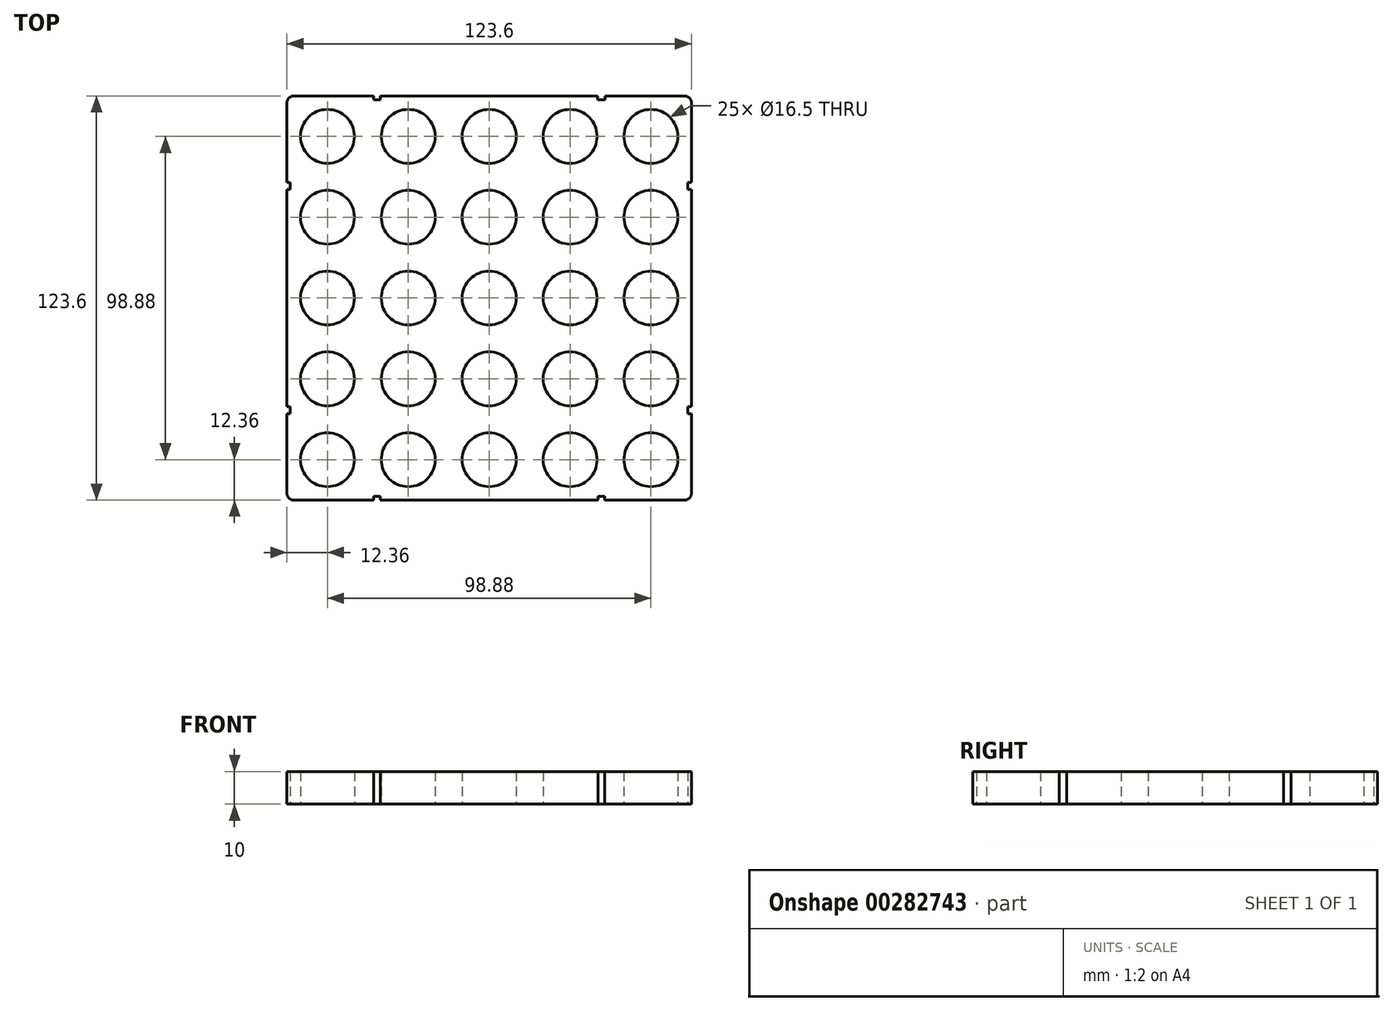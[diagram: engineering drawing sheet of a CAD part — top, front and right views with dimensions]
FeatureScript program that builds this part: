
annotation { "Feature Type Name" : "Feature", "Feature Type Description" : "" }
export const myFeature = defineFeature(function(context is Context, id is Id, definition is map)
    precondition{}
    {
        {
            var Q0;
            Q0=qCreatedBy(makeId("Top.planeOp"),FACE);
            var sketch = newSketch(context, id + "F0", { "sketchPlane" : qUnion([Q0])});
            skLineSegment(sketch, "E0.bottom", {"start": v(59.8, 61.8) * mm, "end": v(-59.8, 61.8) * mm});
            skLineSegment(sketch, "E0.top", {"start": v(59.8, -61.8) * mm, "end": v(-59.8, -61.8) * mm});
            skLineSegment(sketch, "E0.left", {"start": v(61.8, 59.8) * mm, "end": v(61.8, -59.8) * mm});
            skLineSegment(sketch, "E0.right", {"start": v(-61.8, 59.8) * mm, "end": v(-61.8, -59.8) * mm});
            skPoint(sketch, "E0.middle", {"position": v(0, 0) * mm});
            skPoint(sketch, "E1.visualSharp", {"position": v(-61.8, 61.8) * mm});
            skArc(sketch, "E1.filletArc", {"start": v(-59.8, 61.8) * mm, "mid": v(-61.21, 61.21) * mm, "end": v(-61.8, 59.8) * mm});
            skPoint(sketch, "E2.visualSharp", {"position": v(61.8, 61.8) * mm});
            skArc(sketch, "E2.filletArc", {"start": v(61.8, 59.8) * mm, "mid": v(61.21, 61.21) * mm, "end": v(59.8, 61.8) * mm});
            skPoint(sketch, "E3.visualSharp", {"position": v(61.8, -61.8) * mm});
            skArc(sketch, "E3.filletArc", {"start": v(59.8, -61.8) * mm, "mid": v(61.21, -61.21) * mm, "end": v(61.8, -59.8) * mm});
            skPoint(sketch, "E4.visualSharp", {"position": v(-61.8, -61.8) * mm});
            skArc(sketch, "E4.filletArc", {"start": v(-61.8, -59.8) * mm, "mid": v(-61.21, -61.21) * mm, "end": v(-59.8, -61.8) * mm});
            skLineSegment(sketch, "E5", {"start": v(-78.6, 0) * mm, "end": v(67.95, 0) * mm, "construction": true});
            skLineSegment(sketch, "E6", {"start": v(0, 68.22) * mm, "end": v(0, -54.86) * mm, "construction": true});
            skLineSegment(sketch, "E7", {"start": v(-24.72, 68.22) * mm, "end": v(-24.72, -54.86) * mm, "construction": true});
            skLineSegment(sketch, "E8", {"start": v(-49.44, 68.22) * mm, "end": v(-49.44, -54.86) * mm, "construction": true});
            skLineSegment(sketch, "E9", {"start": v(24.72, 68.22) * mm, "end": v(24.72, -54.86) * mm, "construction": true});
            skLineSegment(sketch, "E10", {"start": v(49.44, 68.22) * mm, "end": v(49.44, -54.86) * mm, "construction": true});
            skLineSegment(sketch, "E11", {"start": v(-78.6, 24.72) * mm, "end": v(67.95, 24.72) * mm, "construction": true});
            skLineSegment(sketch, "E12", {"start": v(-78.6, 49.44) * mm, "end": v(67.95, 49.44) * mm, "construction": true});
            skLineSegment(sketch, "E13", {"start": v(-78.6, -24.72) * mm, "end": v(67.95, -24.72) * mm, "construction": true});
            skLineSegment(sketch, "E14", {"start": v(-78.6, -49.44) * mm, "end": v(67.95, -49.44) * mm, "construction": true});
            skCircle(sketch, "E15", {"center": v(-49.44, 49.44) * mm, "radius": 8.25 * mm});
            skCircle(sketch, "E16", {"center": v(-24.72, 49.44) * mm, "radius": 8.25 * mm});
            skCircle(sketch, "E17", {"center": v(0, 49.44) * mm, "radius": 8.25 * mm});
            skCircle(sketch, "E18", {"center": v(24.72, 49.44) * mm, "radius": 8.25 * mm});
            skCircle(sketch, "E19", {"center": v(49.44, 49.44) * mm, "radius": 8.25 * mm});
            skCircle(sketch, "E20", {"center": v(-49.44, 24.72) * mm, "radius": 8.25 * mm});
            skCircle(sketch, "E21", {"center": v(-24.72, 24.72) * mm, "radius": 8.25 * mm});
            skCircle(sketch, "E22", {"center": v(0, 24.72) * mm, "radius": 8.25 * mm});
            skCircle(sketch, "E23", {"center": v(24.72, 24.72) * mm, "radius": 8.25 * mm});
            skCircle(sketch, "E24", {"center": v(49.44, 24.72) * mm, "radius": 8.25 * mm});
            skCircle(sketch, "E25", {"center": v(49.44, 0) * mm, "radius": 8.25 * mm});
            skCircle(sketch, "E26", {"center": v(24.72, 0) * mm, "radius": 8.25 * mm});
            skCircle(sketch, "E27", {"center": v(-49.44, 0) * mm, "radius": 8.25 * mm});
            skCircle(sketch, "E28", {"center": v(-24.72, 0) * mm, "radius": 8.25 * mm});
            skCircle(sketch, "E29", {"center": v(0, 0) * mm, "radius": 8.25 * mm});
            skCircle(sketch, "E30", {"center": v(-49.44, -24.72) * mm, "radius": 8.25 * mm});
            skCircle(sketch, "E31", {"center": v(-49.44, -49.44) * mm, "radius": 8.25 * mm});
            skCircle(sketch, "E32", {"center": v(-24.72, -24.72) * mm, "radius": 8.25 * mm});
            skCircle(sketch, "E33", {"center": v(-24.72, -49.44) * mm, "radius": 8.25 * mm});
            skCircle(sketch, "E34", {"center": v(0, -24.72) * mm, "radius": 8.25 * mm});
            skCircle(sketch, "E35", {"center": v(0, -49.44) * mm, "radius": 8.25 * mm});
            skCircle(sketch, "E36", {"center": v(24.72, -24.72) * mm, "radius": 8.25 * mm});
            skCircle(sketch, "E37", {"center": v(24.72, -49.44) * mm, "radius": 8.25 * mm});
            skCircle(sketch, "E38", {"center": v(49.44, -24.72) * mm, "radius": 8.25 * mm});
            skCircle(sketch, "E39", {"center": v(49.44, -49.44) * mm, "radius": 8.25 * mm});
            skSolve(sketch);
        }
        {
            var Q0;
            Q0=qCreatedBy(makeId("Top.planeOp"),FACE);
            var sketch = newSketch(context, id + "F1", { "sketchPlane" : qUnion([Q0])});
            skLineSegment(sketch, "E40", {"start": v(-34.3, 79.9) * mm, "end": v(-34.3, -79.91) * mm, "construction": true});
            skLineSegment(sketch, "E41", {"start": v(34.3, -79.91) * mm, "end": v(34.3, 79.84) * mm, "construction": true});
            skLineSegment(sketch, "E42", {"start": v(-79.51, 34.3) * mm, "end": v(79.76, 34.3) * mm, "construction": true});
            skLineSegment(sketch, "E43", {"start": v(-79.78, -34.3) * mm, "end": v(79.98, -34.3) * mm, "construction": true});
            skLineSegment(sketch, "E44.bottom", {"start": v(-33.3, 62.9) * mm, "end": v(-35.3, 62.9) * mm});
            skLineSegment(sketch, "E44.top", {"start": v(-33.3, 60.7) * mm, "end": v(-35.3, 60.7) * mm});
            skLineSegment(sketch, "E44.left", {"start": v(-33.3, 62.9) * mm, "end": v(-33.3, 60.7) * mm});
            skLineSegment(sketch, "E44.right", {"start": v(-35.3, 62.9) * mm, "end": v(-35.3, 60.7) * mm});
            skPoint(sketch, "E44.middle", {"position": v(-34.3, 61.8) * mm});
            skLineSegment(sketch, "E45.bottom", {"start": v(35.4, 62.9) * mm, "end": v(33.2, 62.9) * mm});
            skLineSegment(sketch, "E45.top", {"start": v(35.4, 60.7) * mm, "end": v(33.2, 60.7) * mm});
            skLineSegment(sketch, "E45.left", {"start": v(35.4, 62.9) * mm, "end": v(35.4, 60.7) * mm});
            skLineSegment(sketch, "E45.right", {"start": v(33.2, 62.9) * mm, "end": v(33.2, 60.7) * mm});
            skPoint(sketch, "E45.middle", {"position": v(34.3, 61.8) * mm});
            skLineSegment(sketch, "E46.bottom", {"start": v(62.9, 33.2) * mm, "end": v(60.7, 33.2) * mm});
            skLineSegment(sketch, "E46.top", {"start": v(62.9, 35.4) * mm, "end": v(60.7, 35.4) * mm});
            skLineSegment(sketch, "E46.left", {"start": v(62.9, 33.2) * mm, "end": v(62.9, 35.4) * mm});
            skLineSegment(sketch, "E46.right", {"start": v(60.7, 33.2) * mm, "end": v(60.7, 35.4) * mm});
            skPoint(sketch, "E46.middle", {"position": v(61.8, 34.3) * mm});
            skLineSegment(sketch, "E47.bottom", {"start": v(62.9, -35.4) * mm, "end": v(60.7, -35.4) * mm});
            skLineSegment(sketch, "E47.top", {"start": v(62.9, -33.2) * mm, "end": v(60.7, -33.2) * mm});
            skLineSegment(sketch, "E47.left", {"start": v(62.9, -35.4) * mm, "end": v(62.9, -33.2) * mm});
            skLineSegment(sketch, "E47.right", {"start": v(60.7, -35.4) * mm, "end": v(60.7, -33.2) * mm});
            skPoint(sketch, "E47.middle", {"position": v(61.8, -34.3) * mm});
            skLineSegment(sketch, "E48.bottom", {"start": v(35.3, -62.9) * mm, "end": v(33.3, -62.9) * mm});
            skLineSegment(sketch, "E48.top", {"start": v(35.3, -60.7) * mm, "end": v(33.3, -60.7) * mm});
            skLineSegment(sketch, "E48.left", {"start": v(35.3, -62.9) * mm, "end": v(35.3, -60.7) * mm});
            skLineSegment(sketch, "E48.right", {"start": v(33.3, -62.9) * mm, "end": v(33.3, -60.7) * mm});
            skPoint(sketch, "E48.middle", {"position": v(34.3, -61.8) * mm});
            skLineSegment(sketch, "E49.bottom", {"start": v(-33.3, -62.9) * mm, "end": v(-35.3, -62.9) * mm});
            skLineSegment(sketch, "E49.top", {"start": v(-33.3, -60.7) * mm, "end": v(-35.3, -60.7) * mm});
            skLineSegment(sketch, "E49.left", {"start": v(-33.3, -62.9) * mm, "end": v(-33.3, -60.7) * mm});
            skLineSegment(sketch, "E49.right", {"start": v(-35.3, -62.9) * mm, "end": v(-35.3, -60.7) * mm});
            skPoint(sketch, "E49.middle", {"position": v(-34.3, -61.8) * mm});
            skLineSegment(sketch, "E50.bottom", {"start": v(-60.8, -33.2) * mm, "end": v(-62.8, -33.2) * mm});
            skLineSegment(sketch, "E50.top", {"start": v(-60.8, -35.4) * mm, "end": v(-62.8, -35.4) * mm});
            skLineSegment(sketch, "E50.left", {"start": v(-60.8, -33.2) * mm, "end": v(-60.8, -35.4) * mm});
            skLineSegment(sketch, "E50.right", {"start": v(-62.8, -33.2) * mm, "end": v(-62.8, -35.4) * mm});
            skPoint(sketch, "E50.middle", {"position": v(-61.8, -34.3) * mm});
            skLineSegment(sketch, "E51.bottom", {"start": v(-60.8, 35.4) * mm, "end": v(-62.8, 35.4) * mm});
            skLineSegment(sketch, "E51.top", {"start": v(-60.8, 33.2) * mm, "end": v(-62.8, 33.2) * mm});
            skLineSegment(sketch, "E51.left", {"start": v(-60.8, 35.4) * mm, "end": v(-60.8, 33.2) * mm});
            skLineSegment(sketch, "E51.right", {"start": v(-62.8, 35.4) * mm, "end": v(-62.8, 33.2) * mm});
            skPoint(sketch, "E51.middle", {"position": v(-61.8, 34.3) * mm});
            skSolve(sketch);
        }
        {
            var Q0;
            Q0=makeQuery(id+"F0.imprint","IMPRINT",FACE,{"disambiguationData":[TD([[makeQuery(id+"F0.imprint","IMPRINT",EDGE,{"derivedFrom":sQuery(id+"F0.wireOp",EDGE,"E0.bottom")}),1.0]])]});
            extrude(context, id + "F2", {"entities" : qUnion([Q0]), "depth" : 10 * mm});
        }
        {
            var Q0;
            Q0=qSketchRegion(id+"F1",true);
            extrude(context, id + "F3", {"entities" : qUnion([Q0]), "operationType" : NewBodyOperationType.REMOVE, "depth" : 10 * mm});
        }
    });
